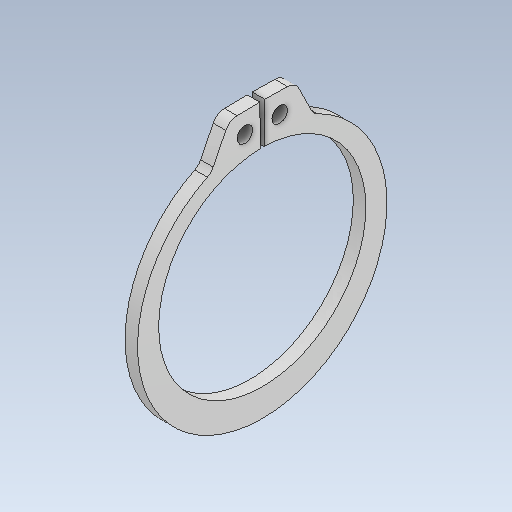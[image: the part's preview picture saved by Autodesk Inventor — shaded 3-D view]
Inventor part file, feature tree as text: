
AUTODESK INVENTOR PART (.ipt)
format: ipt  version: 2020 (Build 240168000, 168)  size: 114,688 bytes
history: native  units: in
note: dims shown in document units (in); Inventor stores cm internally (conversion verified against a paired STEP export)
features: fillet x1
ambient origin geometry x8: Origin, YZ Plane, XZ Plane, XY Plane, X Axis, Y Axis, Z Axis, Center Point
bodies: Solid1 (feature_tree)
feature tree (1):
  fillet  "Fillet1"  [1 undecoded]
note: 1 required parameter value undecoded (feature->parameter linkage not recoverable at this tier; creation-order binding heuristic only, values carry confidence <= 0.55)
